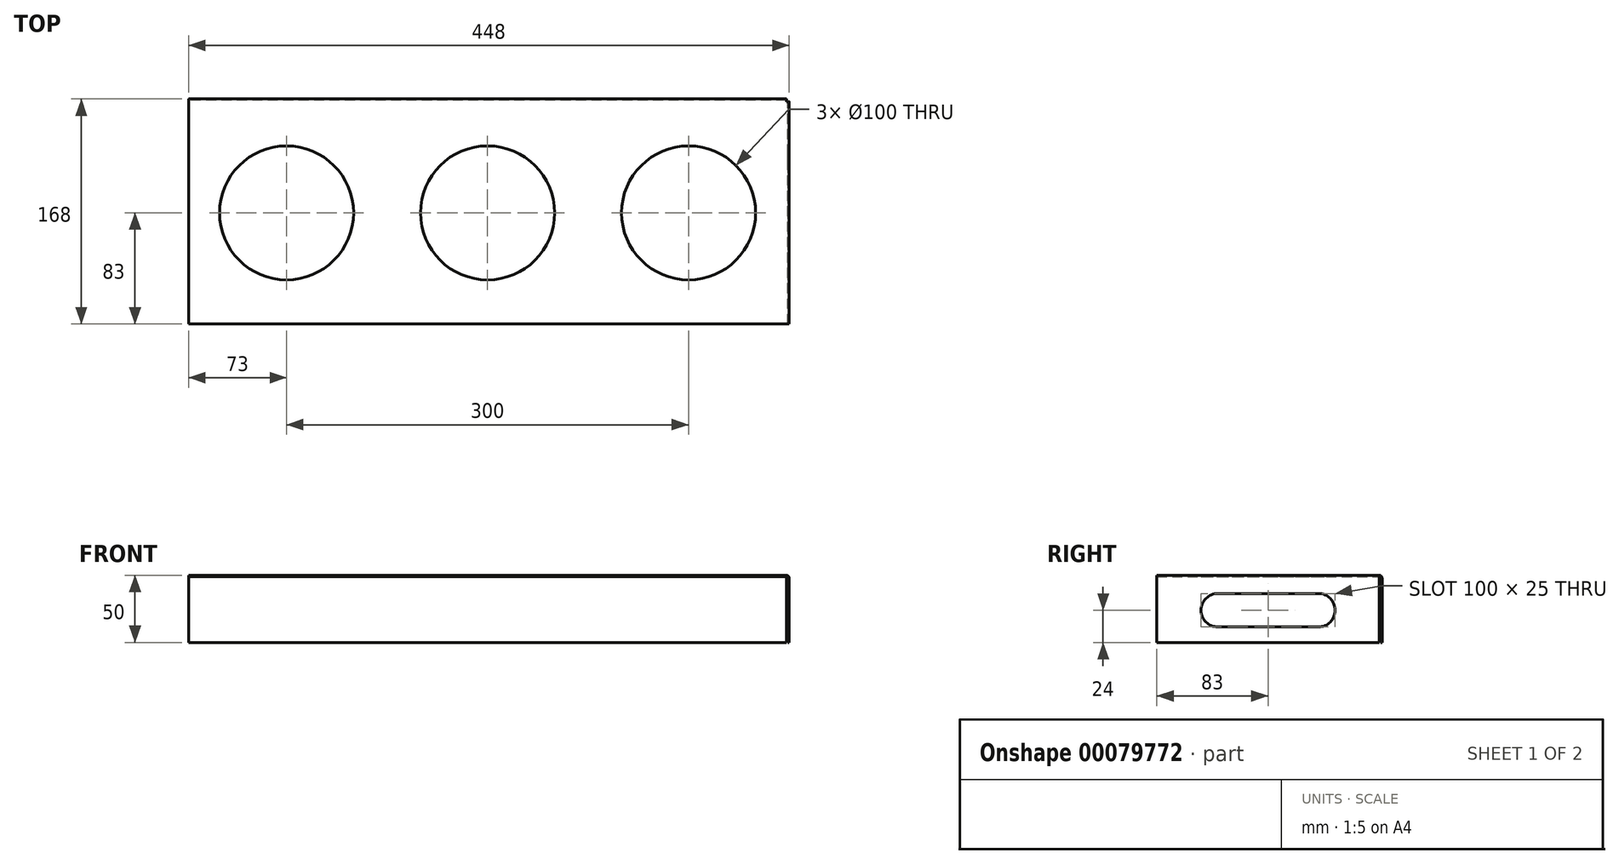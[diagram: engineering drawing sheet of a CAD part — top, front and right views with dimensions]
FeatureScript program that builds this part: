
annotation { "Feature Type Name" : "Feature", "Feature Type Description" : "" }
export const myFeature = defineFeature(function(context is Context, id is Id, definition is map)
    precondition{}
    {
        {
            assignVariable(context, id + "F0", {"name" : "W", "anyValue" : 166});
        }
        {
            assignVariable(context, id + "F1", {"name" : "L", "anyValue" : 446});
        }
        {
            assignVariable(context, id + "F2", {"name" : "t", "anyValue" : 1});
        }
        {
            var Q0;
            Q0=qCreatedBy(makeId("Top.planeOp"),FACE);
            var sketch = newSketch(context, id + "F3", { "sketchPlane" : qUnion([Q0])});
            skLineSegment(sketch, "E0.bottom", {"start": v(223, -83) * mm, "end": v(-223, -83) * mm});
            skLineSegment(sketch, "E0.top", {"start": v(223, 83) * mm, "end": v(-223, 83) * mm});
            skLineSegment(sketch, "E0.left", {"start": v(223, -83) * mm, "end": v(223, 83) * mm});
            skLineSegment(sketch, "E0.right", {"start": v(-223, -83) * mm, "end": v(-223, 83) * mm});
            skPoint(sketch, "E0.middle", {"position": v(0, 0) * mm});
            skCircle(sketch, "E1", {"center": v(0, 0) * mm, "radius": 50 * mm});
            skCircle(sketch, "E2", {"center": v(150, 0) * mm, "radius": 50 * mm});
            skCircle(sketch, "E3", {"center": v(-150, 0) * mm, "radius": 50 * mm});
            skSolve(sketch);
        }
        {
            var Q0;
            Q0=makeQuery(id+"F3.imprint","IMPRINT",FACE,{"disambiguationData":[TD([[makeQuery(id+"F3.imprint","IMPRINT",EDGE,{"derivedFrom":sQuery(id+"F3.wireOp",EDGE,"E0.bottom")}),-1.0]])]});
            extrude(context, id + "F4", {"entities" : qUnion([Q0]), "depth" : (getVariable(context, 't')) * mm});
        }
        {
            var Q0;
            Q0=qCreatedBy(makeId("Right.planeOp"),FACE);
            var sketch = newSketch(context, id + "F5", { "sketchPlane" : qUnion([Q0])});
            skLineSegment(sketch, "E4.0", {"start": v(83, 1) * mm, "end": v(83, 0) * mm});
            skLineSegment(sketch, "E4.1", {"start": v(-83, 1) * mm, "end": v(83, 1) * mm, "construction": true});
            skLineSegment(sketch, "E4.2", {"start": v(-83, 0) * mm, "end": v(83, 0) * mm, "construction": true});
            skArc(sketch, "E5", {"start": v(84, -1) * mm, "mid": v(83.7, -0.3) * mm, "end": v(83, 0) * mm});
            skArc(sketch, "E6", {"start": v(85, -1) * mm, "mid": v(84.41, 0.41) * mm, "end": v(83, 1) * mm});
            skLineSegment(sketch, "E7", {"start": v(84, -1) * mm, "end": v(84, -49) * mm});
            skLineSegment(sketch, "E8", {"start": v(84, -49) * mm, "end": v(85, -49) * mm});
            skLineSegment(sketch, "E9", {"start": v(85, -49) * mm, "end": v(85, -1) * mm});
            skSolve(sketch);
        }
        {
            var Q0;
            Q0 = qSketchRegion(id + "F5", true);
            extrude(context, id + "F6", {"entities" : qUnion([Q0]), "operationType" : NewBodyOperationType.ADD, "endBound" : BoundingType.SYMMETRIC, "depth" : (getVariable(context, 'L')) * mm});
        }
        {
            var Q0;
            Q0=qCreatedBy(makeId("Front.planeOp"),FACE);
            var sketch = newSketch(context, id + "F7", { "sketchPlane" : qUnion([Q0])});
            skLineSegment(sketch, "E10.0", {"start": v(223, 1) * mm, "end": v(-223, 1) * mm, "construction": true});
            skLineSegment(sketch, "E10.1", {"start": v(223, 0) * mm, "end": v(-223, 0) * mm, "construction": true});
            skLineSegment(sketch, "E11", {"start": v(223, 1) * mm, "end": v(223, 0) * mm});
            skArc(sketch, "E12", {"start": v(225, -1) * mm, "mid": v(224.41, 0.41) * mm, "end": v(223, 1) * mm});
            skArc(sketch, "E13", {"start": v(224, -1) * mm, "mid": v(223.7, -0.3) * mm, "end": v(223, 0) * mm});
            skLineSegment(sketch, "E14", {"start": v(224, -1) * mm, "end": v(224, -49) * mm});
            skLineSegment(sketch, "E15", {"start": v(224, -49) * mm, "end": v(225, -49) * mm});
            skLineSegment(sketch, "E16", {"start": v(225, -49) * mm, "end": v(225, -1) * mm});
            skSolve(sketch);
        }
        {
            var Q0;
            Q0 = qSketchRegion(id + "F7", true);
            extrude(context, id + "F8", {"entities" : qUnion([Q0]), "operationType" : NewBodyOperationType.ADD, "endBound" : BoundingType.SYMMETRIC, "depth" : (getVariable(context, 'W')) * mm});
        }
        {
            var Q0;
            Q0=qCreatedBy(makeId("Right.planeOp"),FACE);
            var sketch = newSketch(context, id + "F9", { "sketchPlane" : qUnion([Q0])});
            skLineSegment(sketch, "E17", {"start": v(37.5, -25) * mm, "end": v(-37.5, -25) * mm, "construction": true});
            skPoint(sketch, "E18", {"position": v(0, -25) * mm});
            skArc(sketch, "E19.0.startCap", {"start": v(37.5, -12.5) * mm, "mid": v(50, -25) * mm, "end": v(37.5, -37.5) * mm});
            skArc(sketch, "E19.0.endCap", {"start": v(-37.5, -37.5) * mm, "mid": v(-50, -25) * mm, "end": v(-37.5, -12.5) * mm});
            skLineSegment(sketch, "E19.0.left", {"start": v(37.5, -37.5) * mm, "end": v(-37.5, -37.5) * mm});
            skLineSegment(sketch, "E19.0.right", {"start": v(37.5, -12.5) * mm, "end": v(-37.5, -12.5) * mm});
            skSolve(sketch);
        }
        {
            var Q0;
            Q0 = qSketchRegion(id + "F9", true);
            extrude(context, id + "F10", {"entities" : qUnion([Q0]), "operationType" : NewBodyOperationType.REMOVE, "endBound" : BoundingType.THROUGH_ALL, "oppositeDirection" : true, "depth" : 25 * mm, "hasSecondDirection" : true, "secondDirectionBound" : SecondDirectionBoundingType.THROUGH_ALL, "secondDirectionOppositeDirection" : false, "secondDirectionDepth" : 25 * mm});
        }
    });
